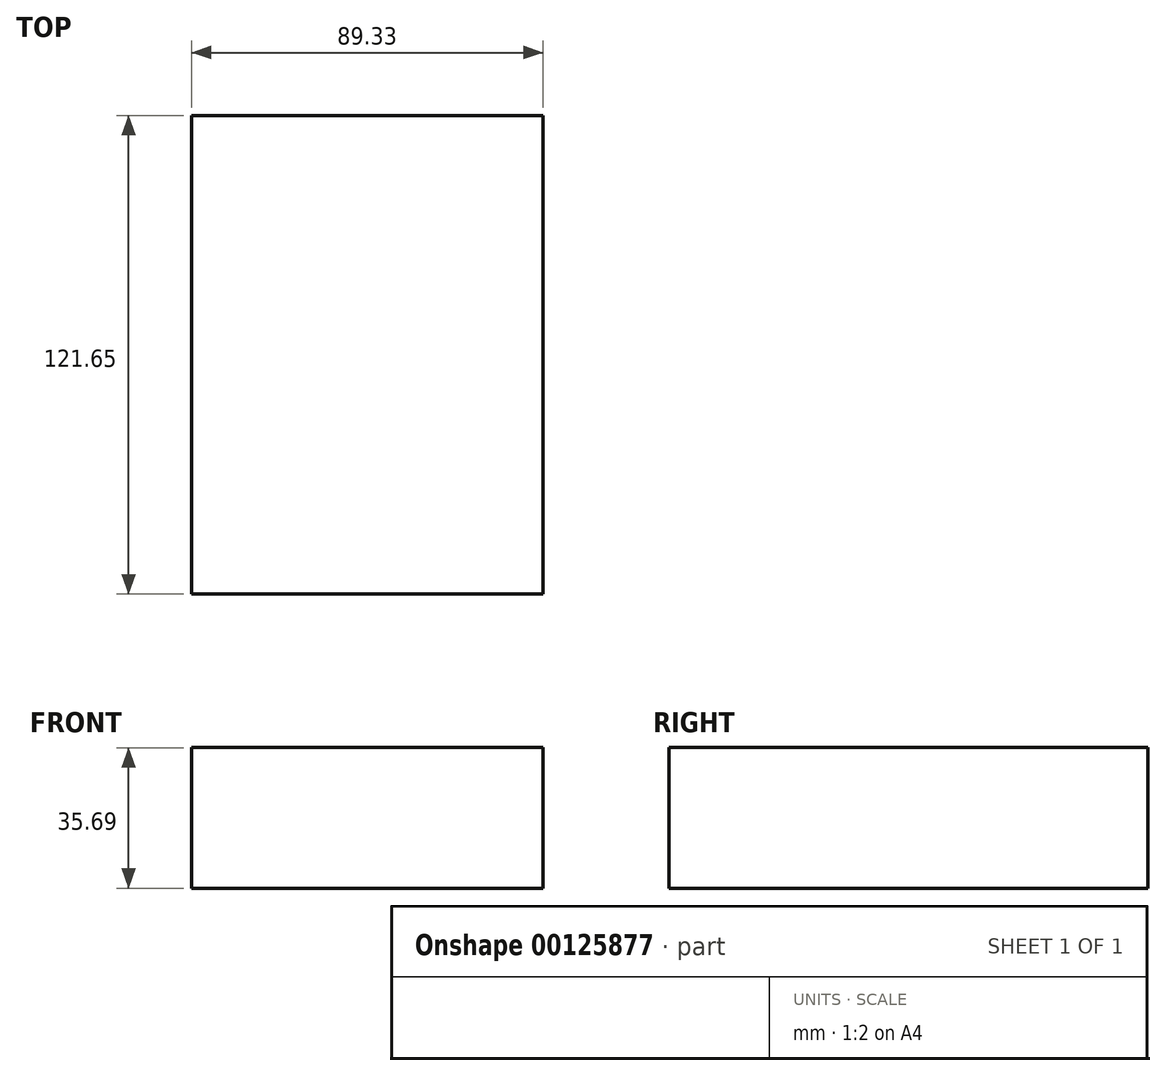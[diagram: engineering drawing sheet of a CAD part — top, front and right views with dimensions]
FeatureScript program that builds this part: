
annotation { "Feature Type Name" : "Feature", "Feature Type Description" : "" }
export const myFeature = defineFeature(function(context is Context, id is Id, definition is map)
    precondition{}
    {
        {
            var Q0;
            Q0=qCreatedBy(makeId("Front.planeOp"),FACE);
            var sketch = newSketch(context, id + "F0", { "sketchPlane" : qUnion([Q0])});
            skLineSegment(sketch, "E0.bottom", {"start": v(-40.84, 35.7) * mm, "end": v(48.5, 35.7) * mm});
            skLineSegment(sketch, "E0.top", {"start": v(-40.84, 0) * mm, "end": v(48.5, 0) * mm});
            skLineSegment(sketch, "E0.left", {"start": v(-40.84, 35.7) * mm, "end": v(-40.84, 0) * mm});
            skLineSegment(sketch, "E0.right", {"start": v(48.5, 35.7) * mm, "end": v(48.5, 0) * mm});
            skSolve(sketch);
        }
        {
            var Q0;
            Q0 = qSketchRegion(id + "F0", true);
            extrude(context, id + "F1", {"entities" : qUnion([Q0]), "oppositeDirection" : true, "depth" : 121.65 * mm});
        }
    });
